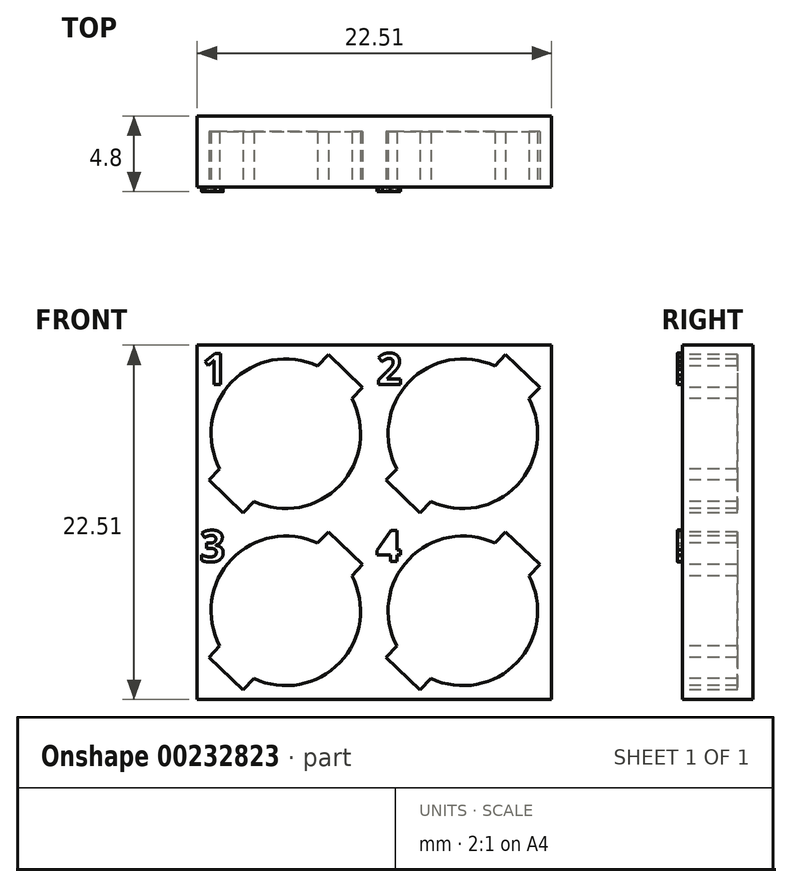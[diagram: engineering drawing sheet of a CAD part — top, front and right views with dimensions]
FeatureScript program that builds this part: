
annotation { "Feature Type Name" : "Feature", "Feature Type Description" : "" }
export const myFeature = defineFeature(function(context is Context, id is Id, definition is map)
    precondition{}
    {
        {
            var Q0;
            Q0=qCreatedBy(makeId("Front.planeOp"),FACE);
            var sketch = newSketch(context, id + "F0", { "sketchPlane" : qUnion([Q0])});
            skLineSegment(sketch, "E0.bottom", {"start": v(5.63, -5.62) * mm, "end": v(-5.62, -5.63) * mm});
            skLineSegment(sketch, "E0.top", {"start": v(5.62, 5.63) * mm, "end": v(-5.63, 5.62) * mm});
            skLineSegment(sketch, "E0.left", {"start": v(5.63, -5.62) * mm, "end": v(5.62, 5.63) * mm});
            skLineSegment(sketch, "E0.right", {"start": v(-5.62, -5.63) * mm, "end": v(-5.63, 5.62) * mm});
            skPoint(sketch, "E0.middle", {"position": v(0, 0) * mm});
            skSolve(sketch);
        }
        {
            var Q0;
            Q0 = qSketchRegion(id + "F0", true);
            extrude(context, id + "F1", {"entities" : qUnion([Q0]), "oppositeDirection" : true, "depth" : 4.5 * mm, "offsetDistance" : 25 * mm});
        }
        {
            var Q0;
            Q0=qCreatedBy(makeId("Front.planeOp"),FACE);
            var sketch = newSketch(context, id + "F2", { "sketchPlane" : qUnion([Q0])});
            skCircle(sketch, "E1", {"center": v(0, 0) * mm, "radius": 4.75 * mm});
            skLineSegment(sketch, "E2", {"start": v(2.02, 4.3) * mm, "end": v(2.71, 5.02) * mm});
            skLineSegment(sketch, "E3", {"start": v(2.71, 5.02) * mm, "end": v(4.89, 2.95) * mm});
            skLineSegment(sketch, "E4", {"start": v(4.89, 2.95) * mm, "end": v(4.2, 2.23) * mm});
            skLineSegment(sketch, "E5", {"start": v(-4.2, -2.23) * mm, "end": v(-4.89, -2.95) * mm});
            skLineSegment(sketch, "E6", {"start": v(-4.89, -2.95) * mm, "end": v(-2.71, -5.02) * mm});
            skLineSegment(sketch, "E7", {"start": v(-2.71, -5.02) * mm, "end": v(-2.02, -4.3) * mm});
            skSolve(sketch);
        }
        {
            var Q0;
            Q0 = qSketchRegion(id + "F2", true);
            extrude(context, id + "F3", {"entities" : qUnion([Q0]), "operationType" : NewBodyOperationType.REMOVE, "oppositeDirection" : true, "depth" : 3.5 * mm, "offsetDistance" : 25 * mm});
        }
        {
            var Q0;
            Q0=makeQuery(id+"F1.opExtrude","SWEPT_BODY",BODY,{"disambiguationData":[OSD([sQuery(id+"F0.wireOp",EDGE,"E0.bottom"),sQuery(id+"F0.wireOp",EDGE,"E0.top"),sQuery(id+"F0.wireOp",EDGE,"E0.left"),sQuery(id+"F0.wireOp",EDGE,"E0.right")])]});
            transform(context, id + "F4", {"entities" : qUnion([Q0]), "transformType" : TransformType.TRANSLATION_3D, "dx" : -11.25 * mm, "dy" : 0 * mm, "dz" : 0 * mm, "makeCopy" : true});
        }
        {
            var Q0;
            Q0=makeQuery(id+"F1.opExtrude","SWEPT_BODY",BODY,{"disambiguationData":[OSD([sQuery(id+"F0.wireOp",EDGE,"E0.bottom"),sQuery(id+"F0.wireOp",EDGE,"E0.top"),sQuery(id+"F0.wireOp",EDGE,"E0.left"),sQuery(id+"F0.wireOp",EDGE,"E0.right")])]});
            transform(context, id + "F5", {"entities" : qUnion([Q0]), "transformType" : TransformType.TRANSLATION_3D, "dx" : 0 * mm, "dy" : 0 * mm, "dz" : 11.25 * mm, "makeCopy" : true});
        }
        {
            var Q0;
            Q0=makeQuery(id+"F1.opExtrude","SWEPT_BODY",BODY,{"disambiguationData":[OSD([sQuery(id+"F0.wireOp",EDGE,"E0.bottom"),sQuery(id+"F0.wireOp",EDGE,"E0.top"),sQuery(id+"F0.wireOp",EDGE,"E0.left"),sQuery(id+"F0.wireOp",EDGE,"E0.right")])]});
            transform(context, id + "F6", {"entities" : qUnion([Q0]), "transformType" : TransformType.TRANSLATION_3D, "dx" : -11.25 * mm, "dy" : 0 * mm, "dz" : 11.25 * mm, "makeCopy" : true});
        }
        {
            var Q0;
            Q0=makeQuery(id+"F1.opExtrude","SWEPT_BODY",BODY,{"disambiguationData":[OSD([sQuery(id+"F0.wireOp",EDGE,"E0.bottom"),sQuery(id+"F0.wireOp",EDGE,"E0.top"),sQuery(id+"F0.wireOp",EDGE,"E0.left"),sQuery(id+"F0.wireOp",EDGE,"E0.right")])]});
            var Q1;
            Q1=makeQuery(id+"F4.opPattern","COPY",BODY,{"derivedFrom":makeQuery(id+"F1.opExtrude","SWEPT_BODY",BODY,{"disambiguationData":[OSD([sQuery(id+"F0.wireOp",EDGE,"E0.bottom"),sQuery(id+"F0.wireOp",EDGE,"E0.top"),sQuery(id+"F0.wireOp",EDGE,"E0.left"),sQuery(id+"F0.wireOp",EDGE,"E0.right")])]}),"instanceName":"1"});
            var Q2;
            Q2=makeQuery(id+"F5.opPattern","COPY",BODY,{"derivedFrom":makeQuery(id+"F1.opExtrude","SWEPT_BODY",BODY,{"disambiguationData":[OSD([sQuery(id+"F0.wireOp",EDGE,"E0.bottom"),sQuery(id+"F0.wireOp",EDGE,"E0.top"),sQuery(id+"F0.wireOp",EDGE,"E0.left"),sQuery(id+"F0.wireOp",EDGE,"E0.right")])]}),"instanceName":"1"});
            var Q3;
            Q3=makeQuery(id+"F6.opPattern","COPY",BODY,{"derivedFrom":makeQuery(id+"F1.opExtrude","SWEPT_BODY",BODY,{"disambiguationData":[OSD([sQuery(id+"F0.wireOp",EDGE,"E0.bottom"),sQuery(id+"F0.wireOp",EDGE,"E0.top"),sQuery(id+"F0.wireOp",EDGE,"E0.left"),sQuery(id+"F0.wireOp",EDGE,"E0.right")])]}),"instanceName":"1"});
            booleanBodies(context, id + "F7", {"operationType" : BooleanOperationType.UNION, "tools" : qUnion([Q0, Q1, Q2, Q3])});
        }
        {
            var Q0;
            {var subQ0=makeQuery(id+"F1.opExtrude","CAP_FACE",FACE,{"disambiguationData":[OSD([sQuery(id+"F0.wireOp",EDGE,"E0.bottom"),sQuery(id+"F0.wireOp",EDGE,"E0.top"),sQuery(id+"F0.wireOp",EDGE,"E0.left"),sQuery(id+"F0.wireOp",EDGE,"E0.right")])],"isStart":true});Q0=makeQuery(id+"F7.opBoolean","MERGE",FACE,{"derivedFrom":[subQ0,makeQuery(id+"F4.opPattern","COPY",FACE,{"derivedFrom":subQ0,"instanceName":"1"}),makeQuery(id+"F5.opPattern","COPY",FACE,{"derivedFrom":subQ0,"instanceName":"1"}),makeQuery(id+"F6.opPattern","COPY",FACE,{"derivedFrom":subQ0,"instanceName":"1"})]});}
            var sketch = newSketch(context, id + "F8", { "sketchPlane" : qUnion([Q0])});
            skText(sketch, "E8", { "text": "1", "fontName": "OpenSans-Bold.ttf"});
            skPoint(sketch, "E8.secondSnap0", {"position": v(-6.67, 14.37) * mm});
            skText(sketch, "E9", { "text": "2", "fontName": "OpenSans-Bold.ttf"});
            skPoint(sketch, "E9.secondSnap0", {"position": v(-3.26, 14.37) * mm});
            skText(sketch, "E10", { "text": "3", "fontName": "OpenSans-Bold.ttf"});
            skPoint(sketch, "E10.secondSnap0", {"position": v(-14.69, 3.28) * mm});
            skText(sketch, "E11", { "text": "4", "fontName": "OpenSans-Bold.ttf"});
            const initialGuessF8  = {"E8": [-0.01654, 0.01437, 1, 0, 0.002], "E9": [-0.00546, 0.01437, 1, 0, 0.002], "E10": [-0.0167, 0.00312, 1, 0, 0.002], "E11": [-0.00549, 0.00313, 1, 0, 0.002]};
            skSetInitialGuess(sketch, initialGuessF8);
            skSolve(sketch);
        }
        {
            var Q0;
            Q0 = qSketchRegion(id + "F8", true);
            extrude(context, id + "F9", {"entities" : qUnion([Q0]), "operationType" : NewBodyOperationType.ADD, "depth" : 0.3 * mm, "offsetDistance" : 25 * mm});
        }
        {
            var Q0;
            Q0=makeQuery(id+"F8.imprint","IMPRINT",FACE,{"disambiguationData":[TD([[makeQuery(id+"F8.imprint","IMPRINT",EDGE,{"derivedFrom":sQuery(id+"F8.wireOp",EDGE,"E11.sketch_text.stroke-11")}),1.0]])]});
            var Q1;
            Q1=makeQuery(id+"F9.opExtrude","CAP_FACE",FACE,{"disambiguationData":[OSD([sQuery(id+"F8.wireOp",EDGE,"E11.sketch_text.stroke-0"),sQuery(id+"F8.wireOp",EDGE,"E11.sketch_text.stroke-1"),sQuery(id+"F8.wireOp",EDGE,"E11.sketch_text.stroke-2"),sQuery(id+"F8.wireOp",EDGE,"E11.sketch_text.stroke-3"),sQuery(id+"F8.wireOp",EDGE,"E11.sketch_text.stroke-4"),sQuery(id+"F8.wireOp",EDGE,"E11.sketch_text.stroke-5"),sQuery(id+"F8.wireOp",EDGE,"E11.sketch_text.stroke-6"),sQuery(id+"F8.wireOp",EDGE,"E11.sketch_text.stroke-7"),sQuery(id+"F8.wireOp",EDGE,"E11.sketch_text.stroke-8"),sQuery(id+"F8.wireOp",EDGE,"E11.sketch_text.stroke-9"),sQuery(id+"F8.wireOp",EDGE,"E11.sketch_text.stroke-10"),sQuery(id+"F8.wireOp",EDGE,"E11.sketch_text.stroke-11"),sQuery(id+"F8.wireOp",EDGE,"E11.sketch_text.stroke-12"),sQuery(id+"F8.wireOp",EDGE,"E11.sketch_text.stroke-13"),sQuery(id+"F8.wireOp",EDGE,"E11.sketch_text.stroke-14"),sQuery(id+"F8.wireOp",EDGE,"E11.sketch_text.stroke-15"),sQuery(id+"F8.wireOp",EDGE,"E11.sketch_text.stroke-16"),sQuery(id+"F8.wireOp",EDGE,"E11.sketch_text.stroke-17")])],"isStart":false});
            extrude(context, id + "F10", {"entities" : qUnion([Q0]), "operationType" : NewBodyOperationType.ADD, "endBound" : BoundingType.UP_TO_SURFACE, "endBoundEntityFace" : qUnion([Q1]), "depth" : 25 * mm, "offsetDistance" : 25 * mm});
        }
    });
